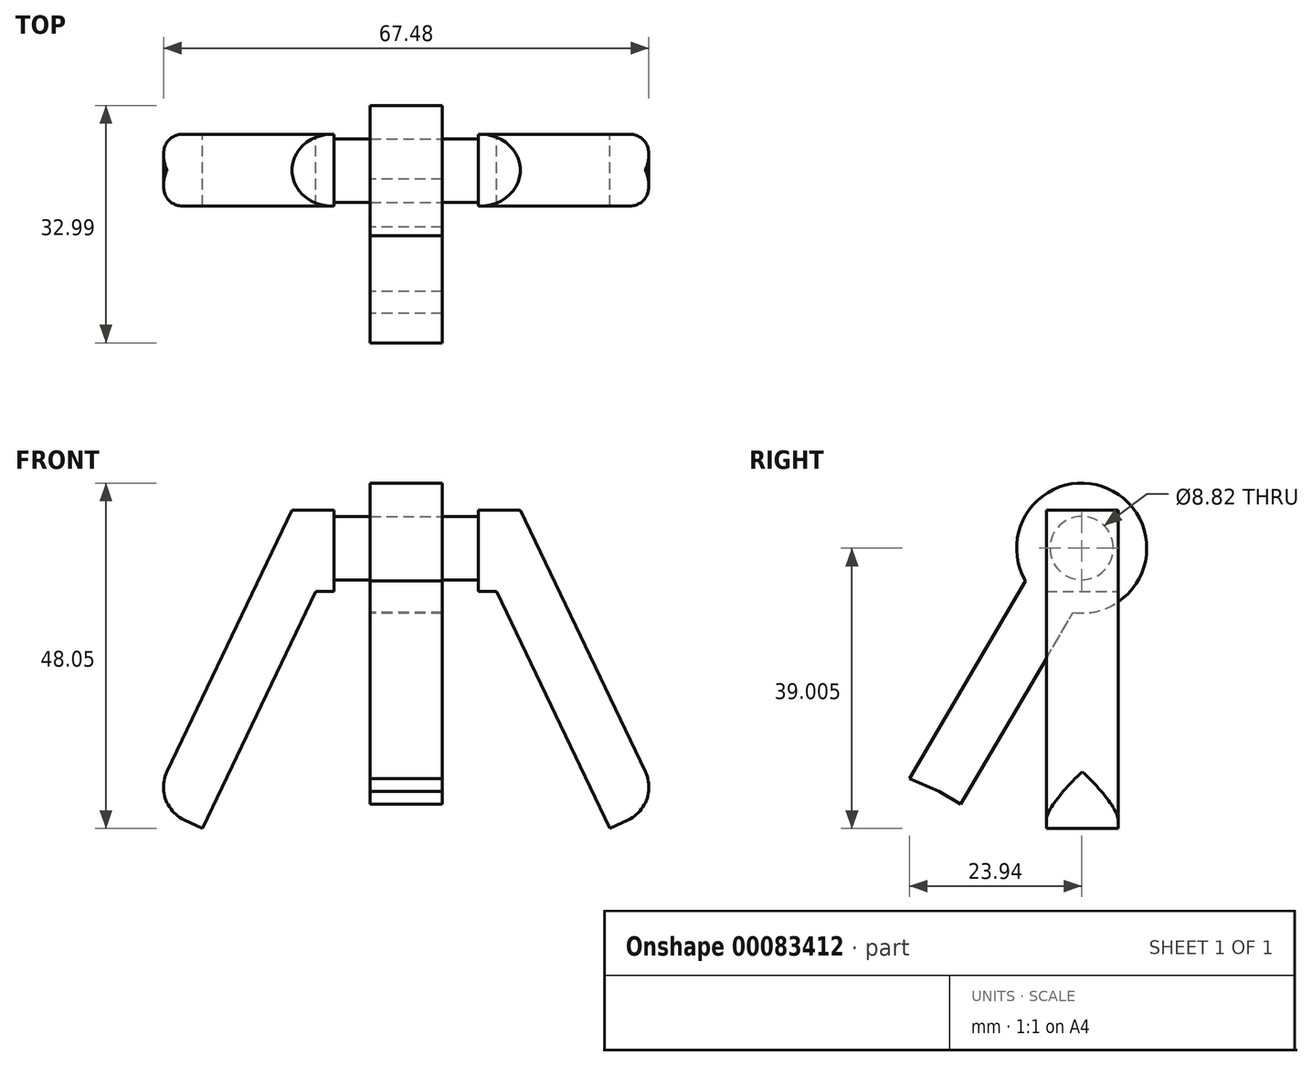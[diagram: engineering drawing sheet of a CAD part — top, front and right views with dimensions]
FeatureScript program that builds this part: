
annotation { "Feature Type Name" : "Feature", "Feature Type Description" : "" }
export const myFeature = defineFeature(function(context is Context, id is Id, definition is map)
    precondition{}
    {
        {
            var Q0;
            Q0=qCreatedBy(makeId("Front.planeOp"),FACE);
            var sketch = newSketch(context, id + "F0", { "sketchPlane" : qUnion([Q0])});
            skLineSegment(sketch, "E0", {"start": v(0, 29.6) * mm, "end": v(0, 40.9) * mm});
            skLineSegment(sketch, "E1", {"start": v(0, 40.9) * mm, "end": v(-15.87, 40.9) * mm});
            skLineSegment(sketch, "E2", {"start": v(-15.87, 40.9) * mm, "end": v(-35.4, 0) * mm});
            skLineSegment(sketch, "E3", {"start": v(-35.4, 0) * mm, "end": v(-28.32, -3.38) * mm});
            skLineSegment(sketch, "E4", {"start": v(-28.32, -3.38) * mm, "end": v(-12.56, 29.6) * mm});
            skLineSegment(sketch, "E5", {"start": v(-12.56, 29.6) * mm, "end": v(0, 29.6) * mm});
            skSolve(sketch);
        }
        {
            var Q0;
            Q0 = qSketchRegion(id + "F0", true);
            var Q1;
            Q1=makeQuery(id+"F0.imprint","IMPRINT",FACE,{"disambiguationData":[TD([[makeQuery(id+"F0.imprint","IMPRINT",EDGE,{"derivedFrom":sQuery(id+"F0.wireOp",EDGE,"E0")}),1.0]])]});
            extrude(context, id + "F1", {"entities" : qUnion([Q0, Q1]), "depth" : 10 * mm});
        }
        {
            var Q0;
            Q0=makeQuery(id+"F1.opExtrude","SWEPT_FACE",FACE,{"disambiguationData":[OSD([sQuery(id+"F0.wireOp",EDGE,"E0")])]});
            var sketch = newSketch(context, id + "F2", { "sketchPlane" : qUnion([Q0])});
            skCircle(sketch, "E6", {"center": v(-5.08, 35.62) * mm, "radius": 4.4 * mm});
            skCircle(sketch, "E7", {"center": v(-5.08, 35.62) * mm, "radius": 9.05 * mm});
            skLineSegment(sketch, "E8", {"start": v(-5.08, 35.62) * mm, "end": v(-24.9, 1.77) * mm});
            skLineSegment(sketch, "E9", {"start": v(-12.9, 31.08) * mm, "end": v(-29.02, 3.55) * mm});
            skLineSegment(sketch, "E10", {"start": v(-29.02, 3.55) * mm, "end": v(-24.9, 1.77) * mm});
            skLineSegment(sketch, "E11", {"start": v(-24.9, 1.77) * mm, "end": v(-21.89, 0) * mm});
            skLineSegment(sketch, "E12", {"start": v(-21.89, 0) * mm, "end": v(-6.28, 26.66) * mm});
            skSolve(sketch);
        }
        {
            var Q0;
            Q0=makeQuery(id+"F2.imprint","IMPRINT",FACE,{"disambiguationData":[TD([[makeQuery(id+"F2.imprint","IMPRINT",EDGE,{"derivedFrom":sQuery(id+"F2.wireOp",EDGE,"E6")}),-1.0]])]});
            extrude(context, id + "F3", {"entities" : qUnion([Q0]), "operationType" : NewBodyOperationType.REMOVE, "oppositeDirection" : true, "depth" : 10.02 * mm});
        }
        {
            var Q0;
            Q0=makeQuery(id+"F1.opExtrude","CAP_EDGE",EDGE,{"disambiguationData":[OSD([sQuery(id+"F0.wireOp",EDGE,"E2")])],"isStart":false});
            var Q1;
            Q1=makeQuery(id+"F1.opExtrude","CAP_EDGE",EDGE,{"disambiguationData":[OSD([sQuery(id+"F0.wireOp",EDGE,"E2")])],"isStart":true});
            var Q2;
            Q2=makeQuery(id+"F1.opExtrude","SWEPT_EDGE",EDGE,{"disambiguationData":[OSD([sQuery(id+"F0.wireOp",EDGE,"E2"),sQuery(id+"F0.wireOp",EDGE,"E3")])]});
            fillet(context, id + "F4", {"entities" : qUnion([Q0, Q1, Q2]), "radius" : 5 * mm, "tangentPropagation" : true, "allowEdgeOverflow" : false});
        }
        {
            var Q0;
            Q0=makeQuery(id+"F1.opExtrude","SWEPT_BODY",BODY,{"disambiguationData":[OSD([sQuery(id+"F0.wireOp",EDGE,"E0"),sQuery(id+"F0.wireOp",EDGE,"E1"),sQuery(id+"F0.wireOp",EDGE,"E2"),sQuery(id+"F0.wireOp",EDGE,"E3"),sQuery(id+"F0.wireOp",EDGE,"E4"),sQuery(id+"F0.wireOp",EDGE,"E5")])]});
            var Q1;
            Q1=makeQuery(id+"F1.opExtrude","SWEPT_FACE",FACE,{"disambiguationData":[OSD([sQuery(id+"F0.wireOp",EDGE,"E0")])]});
            mirror(context, id + "F5", {"operationType" : NewBodyOperationType.ADD, "entities" : qUnion([Q0]), "mirrorPlane" : qUnion([Q1])});
        }
        {
            var Q0;
            {var subQ0=sQuery(id+"F0.wireOp",EDGE,"E0");var subQ5=makeQuery(id+"F1.opExtrude","CAP_EDGE",EDGE,{"disambiguationData":[OSD([subQ0])],"isStart":true});Q0=makeQuery(id+"F2.imprint","IMPRINT",FACE,{"disambiguationData":[TD([[makeQuery(id+"F2.imprint","IMPRINT",EDGE,{"derivedFrom":subQ5}),-1.0]])]});}
            var Q1;
            {var subQ0=sQuery(id+"F2.wireOp",EDGE,"E9");Q1=makeQuery(id+"F2.imprint","IMPRINT",FACE,{"disambiguationData":[TD([[makeQuery(id+"F2.imprint","IMPRINT",EDGE,{"derivedFrom":subQ0}),1.0]])]});}
            var Q2;
            {var subQ4=sQuery(id+"F2.wireOp",EDGE,"E11");Q2=makeQuery(id+"F2.imprint","IMPRINT",FACE,{"disambiguationData":[TD([[makeQuery(id+"F2.imprint","IMPRINT",EDGE,{"derivedFrom":subQ4}),1.0]])]});}
            var Q3;
            Q3=makeQuery(id+"F2.imprint","IMPRINT",FACE,{"disambiguationData":[TD([[makeQuery(id+"F2.imprint","IMPRINT",EDGE,{"derivedFrom":sQuery(id+"F2.wireOp",EDGE,"E6")}),-1.0]])]});
            extrude(context, id + "F6", {"entities" : qUnion([Q0, Q1, Q2, Q3]), "endBound" : BoundingType.SYMMETRIC, "depth" : 10 * mm});
        }
    });
